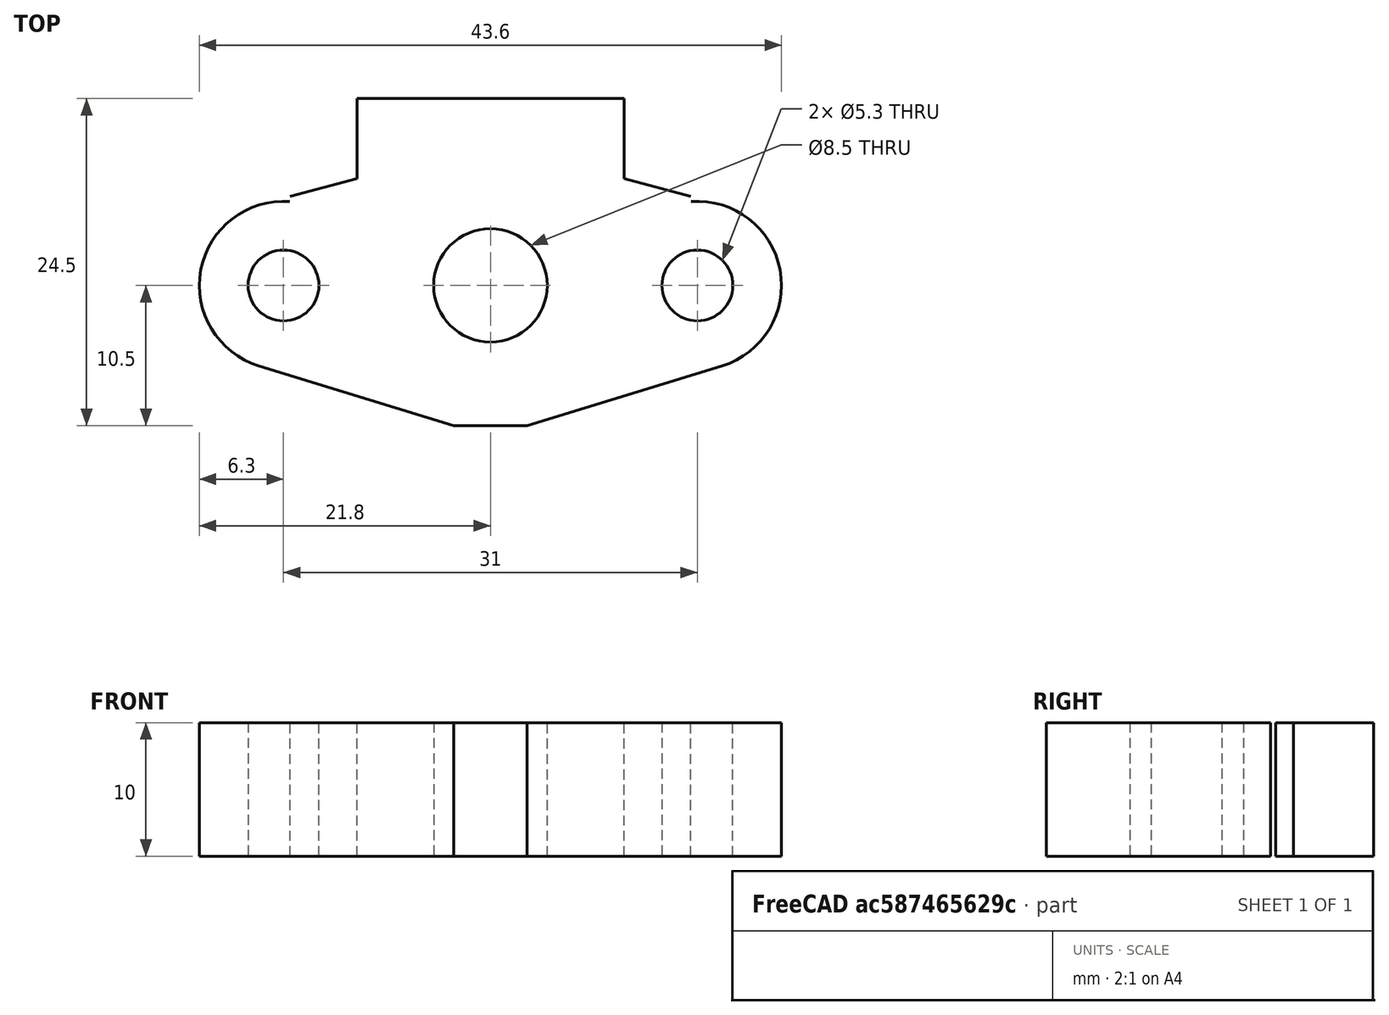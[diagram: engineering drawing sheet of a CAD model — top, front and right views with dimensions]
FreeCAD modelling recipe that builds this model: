
FCSTD DOCUMENT  (FreeCAD 0.19R24276 (Git))
Label: Axis_fix_d8_h10
License: All rights reserved
LicenseURL: http://en.wikipedia.org/wiki/All_rights_reserved
objects: Sketcher::SketchObject×1, PartDesign::Pad×1, PartDesign::Body×1
note: 4 computed .brp shape members not serialized (recipe doc carries the construction recipe); baked Part::Feature solids carry a one-line shape summary decoded from their .brp

FEATURE [Sketcher::SketchObject] Sketch  label="Sketch_d50_kontur"
  FullyConstrained = false
  MapMode = 5
  Support = -> [XY_Plane]
  sketch-geometry (29):
    g0: Circle CenterX=0 CenterY=0 CenterZ=0 NormalX=0 NormalY=0 NormalZ=1 AngleXU=0 Radius=4.25
    g1: Circle CenterX=15.5 CenterY=0 CenterZ=0 NormalX=0 NormalY=0 NormalZ=1 AngleXU=0 Radius=2.65
    g2: Circle CenterX=-15.5 CenterY=0 CenterZ=0 NormalX=0 NormalY=0 NormalZ=1 AngleXU=0 Radius=2.65
    g3: ArcOfCircle CenterX=15.5 CenterY=0 CenterZ=0 NormalX=0 NormalY=0 NormalZ=1 AngleXU=0 Radius=6.3 StartAngle=5.00998 EndAngle=7.59165
    g4: ArcOfCircle CenterX=-15.5 CenterY=0 CenterZ=0 NormalX=0 NormalY=0 NormalZ=1 AngleXU=0 Radius=6.3 StartAngle=1.83312 EndAngle=4.4148
    g5: LineSegment StartX=-10 StartY=14 StartZ=0 EndX=10 EndY=14 EndZ=0
    g6: LineSegment StartX=10 StartY=14 StartZ=0 EndX=10 EndY=8 EndZ=0
    g7: LineSegment StartX=-10 StartY=14 StartZ=0 EndX=-10 EndY=8 EndZ=0
    g8: LineSegment StartX=0 StartY=0 StartZ=0 EndX=0 EndY=14 EndZ=0
    g9: LineSegment StartX=-17.1338 StartY=6.08447 StartZ=0 EndX=-10 EndY=8 EndZ=0
    g10: LineSegment StartX=-15.5 StartY=0 StartZ=0 EndX=-17.1338 EndY=6.08447 EndZ=0
    g11: LineSegment StartX=17.1338 StartY=6.08447 StartZ=0 EndX=10 EndY=8 EndZ=0
    g12: LineSegment StartX=17.1338 StartY=6.08447 StartZ=0 EndX=15.5 EndY=0 EndZ=0
    g13: LineSegment StartX=0 StartY=0 StartZ=0 EndX=21.8 EndY=0 EndZ=0
    g14: LineSegment StartX=-2.75 StartY=-10.5 StartZ=0 EndX=2.75 EndY=-10.5 EndZ=0
    g15: LineSegment StartX=15.5 StartY=0 StartZ=0 EndX=17.3473 EndY=-6.02309 EndZ=0
    g16: LineSegment StartX=-15.5 StartY=0 StartZ=0 EndX=-17.3473 EndY=-6.02309 EndZ=0
    g17: LineSegment StartX=17.3473 StartY=-6.02309 StartZ=0 EndX=2.75 EndY=-10.5 EndZ=0
    g18: LineSegment StartX=-17.3473 StartY=-6.02309 StartZ=0 EndX=-2.75 EndY=-10.5 EndZ=0
    g19: LineSegment StartX=0 StartY=0 StartZ=0 EndX=0 EndY=-10.5 EndZ=0
    g20: LineSegment StartX=-15 StartY=14 StartZ=0 EndX=-15 EndY=6.65742 EndZ=0
    g21: LineSegment StartX=15 StartY=14 StartZ=0 EndX=15 EndY=6.65742 EndZ=0
    g22: Circle CenterX=0 CenterY=0 CenterZ=0 NormalX=0 NormalY=0 NormalZ=1 AngleXU=0 Radius=25
    g23: LineSegment StartX=-15 StartY=14 StartZ=0 EndX=15 EndY=14 EndZ=0
    g24: LineSegment StartX=-17.1338 StartY=6.08447 StartZ=0 EndX=-15 EndY=6.65742 EndZ=0
    g25: LineSegment StartX=15 StartY=6.65742 StartZ=0 EndX=17.1338 EndY=6.08447 EndZ=0
    g26: LineSegment StartX=-15.5 StartY=0 StartZ=0 EndX=-21.8 EndY=0 EndZ=0
    g27: LineSegment StartX=25 StartY=0 StartZ=0 EndX=35.766 EndY=0 EndZ=0
    g28: LineSegment StartX=-10 StartY=14 StartZ=0 EndX=10 EndY=14 EndZ=0
  constraints (73):
    c: Coincident(g0,g-1)
    c: PointOnObject(g1,g-1)
    c: DistanceX(g2,g1) = 31
    c: Symmetric(g2,g1,g-1)
    c: Diameter(g0) = 8.5
    c: Diameter(g1) = 5.3
    c: Equal(g1,g2)
    c: Coincident(g3,g1)
    c: Coincident(g4,g2)
    c: Diameter(g3) = 12.6
    c: Equal(g4,g3)
    c: Horizontal(g5)
    c: DistanceY(g2,g5) = 14
    c: Coincident(g6,g5)
    c: Vertical(g6)
    c: Coincident(g7,g5)
    c: Vertical(g7)
    c: DistanceY(g7,g5) = 6
    c: Equal(g7,g6)
    c: Coincident(g8,g-1)
    c: PointOnObject(g8,g-2)
    c: Symmetric(g5,g5,g8)
    c: DistanceX(g5,g5) = 20
    c: Coincident(g9,g7)
    c: Coincident(g10,g2)
    c: Coincident(g10,g9)
    c: Perpendicular(g10,g9)
    c: Coincident(g11,g6)
    c: Coincident(g12,g11)
    c: Coincident(g12,g1)
    c: Coincident(g13,g-1)
    c: PointOnObject(g27,g-1)
    c: Horizontal(g14)
    c: Coincident(g15,g1)
    c: Coincident(g16,g2)
    c: Coincident(g17,g15)
    c: Coincident(g18,g16)
    c: Perpendicular(g18,g16)
    c: Perpendicular(g17,g15)
    c: Coincident(g18,g14)
    c: Coincident(g14,g17)
    c: DistanceY(g14,g-1) = 10.5
    c: DistanceX(g14,g14) = 5.5
    c: Coincident(g19,g-1)
    c: PointOnObject(g19,g-2)
    c: Symmetric(g14,g14,g19)
    c: Vertical(g20)
    c: Vertical(g21)
    c: Symmetric(g20,g21,g8)
    c: Horizontal(g20,g8)
    c: DistanceX(g20,g21) = 30
    c: PointOnObject(g20,g9)
    c: PointOnObject(g21,g11)
    c: Coincident(g22,g-1)
    c: Diameter(g22) = 50
    c: Coincident(g3,g15)
    c: Tangent(g3,g11) = -1.5708
    c: Coincident(g4,g9)
    c: Coincident(g4,g16)
    c: Coincident(g23,g20)
    c: Coincident(g24,g4)
    c: Coincident(g24,g20)
    c: Coincident(g25,g21)
    c: Coincident(g25,g3)
    c: Coincident(g23,g21)
    c: Coincident(g26,g4)
    c: Horizontal(g26)
    c: PointOnObject(g13,g3)
    c: PointOnObject(g27,g22)
    c: Tangent(g13,g27)
    c: PointOnObject(g26,g4)
    c: Coincident(g28,g7)
    c: Coincident(g28,g6)
FEATURE [PartDesign::Pad] Pad  label="Pad_h10"
  Direction = (1,1,1)
  Length = 10
  Length2 = 100
  Profile = -> Sketch
  Type = 0
FEATURE [PartDesign::Body] Body
  Group = -> [Sketch,Pad]
  Origin = -> Origin
  Tip = -> Pad
